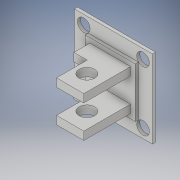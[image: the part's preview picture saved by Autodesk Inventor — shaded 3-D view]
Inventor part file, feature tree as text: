
AUTODESK INVENTOR PART (.ipt)
format: ipt  version: 2018 (Build 220112000, 112)  size: 180,736 bytes
history: native  units: in
note: dims shown in document units (in); Inventor stores cm internally (conversion verified against a paired STEP export)
features: extrude x6, sketch x6
ambient origin geometry x8: Origin, YZ Plane, XZ Plane, XY Plane, X Axis, Y Axis, Z Axis, Center Point
bodies: Solid1 (feature_tree)
feature tree (12):
  extrude  "Extrusion1"  Depth=1.25in
  extrude  "Extrusion2"  Depth=0.225in
  extrude  "Extrusion3"  Depth=0.225in
  extrude  "Extrusion4"  Depth=0.05in TaperAngle=0.0deg
  extrude  "Extrusion5"  Depth=0.075in
  extrude  "Extrusion6"  Depth=0.075in
  sketch  "Sketch1"  dims[d0=1.25in d1=1.25in]
  sketch  "Sketch2"  dims[d2=0.05in d3=0.0in d4=0.225in]
  sketch  "Sketch3"  dims[d5=0.225in d6=0.225in]
  sketch  "Sketch4"  dims[d7=0.225in d8=0.05in d9=0.0in]
  sketch  "Sketch5"  dims[d10=0.075in d11=0.075in]
  sketch  "Sketch6"  dims[d12=0.075in d14=0.075in d15=0.075in d16=0.075in d18=0.75in d19=0.0in d20=0.25in d21=0.3in d22=5.0in d23=0.0in d24=0.2031in d28=0.2031in d29=0.15in d30=0.15in d31=0.15in d32=0.15in d33=0.2031in d34=0.15in d35=0.15in d36=0.2031in d37=0.15in d38=0.15in d39=0.39in d40=0.13in d41=0.13in d42=0.5in d43=0.0in d44=0.4in d45=4.0in d46=0.0in]
